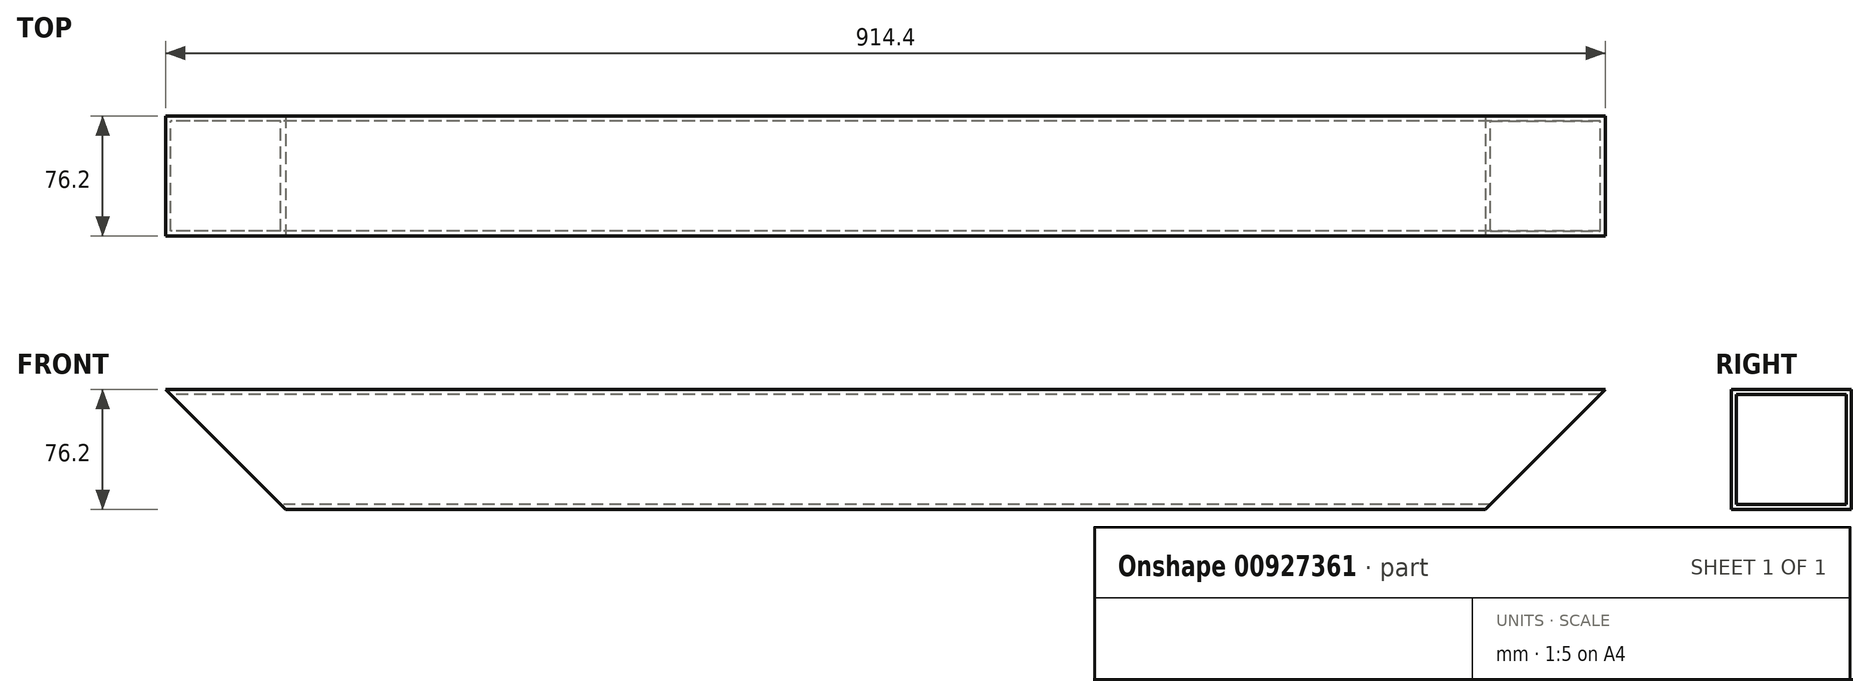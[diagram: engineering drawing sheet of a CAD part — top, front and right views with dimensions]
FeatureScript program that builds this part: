
annotation { "Feature Type Name" : "Feature", "Feature Type Description" : "" }
export const myFeature = defineFeature(function(context is Context, id is Id, definition is map)
    precondition{}
    {
        {
            var Q0;
            Q0=qCreatedBy(makeId("Right.planeOp"),FACE);
            var sketch = newSketch(context, id + "F0", { "sketchPlane" : qUnion([Q0])});
            skLineSegment(sketch, "E0.bottom", {"start": v(-38.1, 38.1) * mm, "end": v(38.1, 38.1) * mm});
            skLineSegment(sketch, "E0.top", {"start": v(-38.1, -38.1) * mm, "end": v(38.1, -38.1) * mm});
            skLineSegment(sketch, "E0.left", {"start": v(-38.1, 38.1) * mm, "end": v(-38.1, -38.1) * mm});
            skLineSegment(sketch, "E0.right", {"start": v(38.1, 38.1) * mm, "end": v(38.1, -38.1) * mm});
            skLineSegment(sketch, "E1.bottom", {"start": v(34.93, 34.92) * mm, "end": v(-34.93, 34.92) * mm});
            skLineSegment(sketch, "E1.top", {"start": v(34.93, -34.92) * mm, "end": v(-34.93, -34.92) * mm});
            skLineSegment(sketch, "E1.left", {"start": v(34.92, 34.92) * mm, "end": v(34.93, -34.93) * mm});
            skLineSegment(sketch, "E1.right", {"start": v(-34.93, 34.92) * mm, "end": v(-34.92, -34.93) * mm});
            skPoint(sketch, "E1.middle", {"position": v(0, 0) * mm});
            skSolve(sketch);
        }
        {
            var Q0;
            Q0=makeQuery(id+"F0.imprint","IMPRINT",FACE,{"disambiguationData":[TD([[makeQuery(id+"F0.imprint","IMPRINT",EDGE,{"derivedFrom":sQuery(id+"F0.wireOp",EDGE,"E0.bottom")}),-1.0]])]});
            extrude(context, id + "F1", {"entities" : qUnion([Q0]), "depth" : 457.2 * mm, "offsetDistance" : 25.4 * mm, "hasSecondDirection" : true, "secondDirectionOppositeDirection" : true, "secondDirectionDepth" : 457.2 * mm});
        }
        {
            var Q0;
            Q0=makeQuery(id+"F1.opExtrude","SWEPT_FACE",FACE,{"disambiguationData":[OSD([sQuery(id+"F0.wireOp",EDGE,"E0.left")])]});
            var sketch = newSketch(context, id + "F2", { "sketchPlane" : qUnion([Q0])});
            skLineSegment(sketch, "E2", {"start": v(-457.2, 38.1) * mm, "end": v(-367.94, -51.16) * mm});
            skLineSegment(sketch, "E3", {"start": v(457.2, 38.1) * mm, "end": v(372.14, -46.96) * mm});
            skSolve(sketch);
        }
        {
            var Q0;
            {var subQ1=sQuery(id+"F0.wireOp",EDGE,"E0.left");var subQ2=makeQuery(id+"F1.opExtrude","CAP_EDGE",EDGE,{"disambiguationData":[OSD([subQ1])],"isStart":true});Q0=makeQuery(id+"F2.imprint","IMPRINT",FACE,{"disambiguationData":[TD([[makeQuery(id+"F2.imprint","IMPRINT",EDGE,{"derivedFrom":subQ2}),1.0]])]});}
            var Q1;
            {var subQ1=sQuery(id+"F0.wireOp",EDGE,"E0.left");var subQ2=makeQuery(id+"F1.opExtrude","CAP_EDGE",EDGE,{"disambiguationData":[OSD([subQ1])],"isStart":false});Q1=makeQuery(id+"F2.imprint","IMPRINT",FACE,{"disambiguationData":[TD([[makeQuery(id+"F2.imprint","IMPRINT",EDGE,{"derivedFrom":subQ2}),-1.0]])]});}
            extrude(context, id + "F3", {"entities" : qUnion([Q0, Q1]), "operationType" : NewBodyOperationType.REMOVE, "endBound" : BoundingType.THROUGH_ALL, "oppositeDirection" : true, "depth" : 25.4 * mm, "offsetDistance" : 25.4 * mm});
        }
    });
